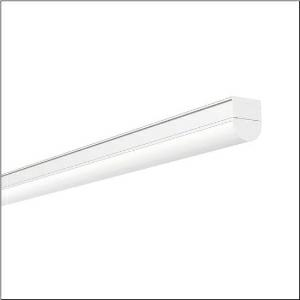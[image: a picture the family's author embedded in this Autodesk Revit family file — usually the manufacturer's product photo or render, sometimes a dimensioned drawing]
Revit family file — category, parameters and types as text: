
# Revit family: ecopack_r__31_51lj12dkm40a_26af
name_source: partatom
category: Lighting Fixtures
units: mm (PartAtom-declared; Revit-internal decimal feet)

## family parameters
Cut with Voids When Loaded = No
Host = Face
Light Source = No
Part Type = Normal
Room Calculation Point = No
Round Connector Dimension = Use Diameter
Shared = No

## types (1)
- --- (1 x LED, 4290 lm, 33 W, 5000K)
    Apparent Load = 33 VA
    CIE Flux Codes = 39 67 87 89 100
    Color Rendering = 80
    Color Temperature = 5000K
    Default Elevation = 1800 mm
    Description = Ecopack® 31, diffuser luminaire, primary optical cover: cover, of PC, frosted, light emission: direct distribution, primary light characteristic: symmetric, installation type: surface-mounted, LED, rated luminous flux: 4.300lm, luminous efficacy: 130lm/W, light colour: 830/840/850, colour temperature: 3000/4000/5000K, control gear: DALI 2, with terminal, 5-pole, mains connection: 220..240V, AC, 50/60Hz, rated input power: 33W, housing, of aluminium, traffic white (RAL 9016), length: 1.150mm, width: 56mm, height: 68mm, end cap, of PC, white, protection rating (complete): IP20, insulation class (complete): insulation class I (protective earthing), certification: CE, impact resistance: IK06, permissible operating ambient temperature: -20..+40°C, packaging unit: 1 piece
    Height = 68 mm
    Lamp = 1 x LED
    Lamp Light Flux = 4290 lm
    Lamp Power = 33 W
    Lamp count = 1
    Length = 1149 mm
    Luminous efficacy = 130 lm/W
    Manufacturer = Siteco
    ModVariant = No
    Model = 51LJ12DKM40A
    Mounting Place = Ceiling
    Mounting Type = Surface mounted
    Number of Poles = 1
    OnlyDefault = Yes
    Power Factor = 1
    Product Name = Ecopack® 31
    Product group = diffuser luminaire
    ProductGroupID = 307
    Protection Class = Protection class I
    Protection Degree = IP 20
    RLX_Detail_Level = 1
    RLX_Emergency_Light_Flux = 0 lm
    RLX_Emergency_Type = 0
    RLX_Emergency_Type_DB = No
    RlxData = <blob elided: 24897 chars, md5=b66dfb24>
    Socket = socket
    Standby Power = 0 W
    System Light Flux = 4290 lm
    System Power = 33 W
    Type Comments = individual setting: colour temperature 5000K
    Type Image = l_1007030.jpg
    URL = http://relux.com
    VarID = @adj_195473
    Voltage = 0 V
    Weight = 0.00 kg
    Width = 56 mm

## geometry (parser evidence)
native form markers: Blend x4, Sweep x12
no freeform markers — native parametric forms only
